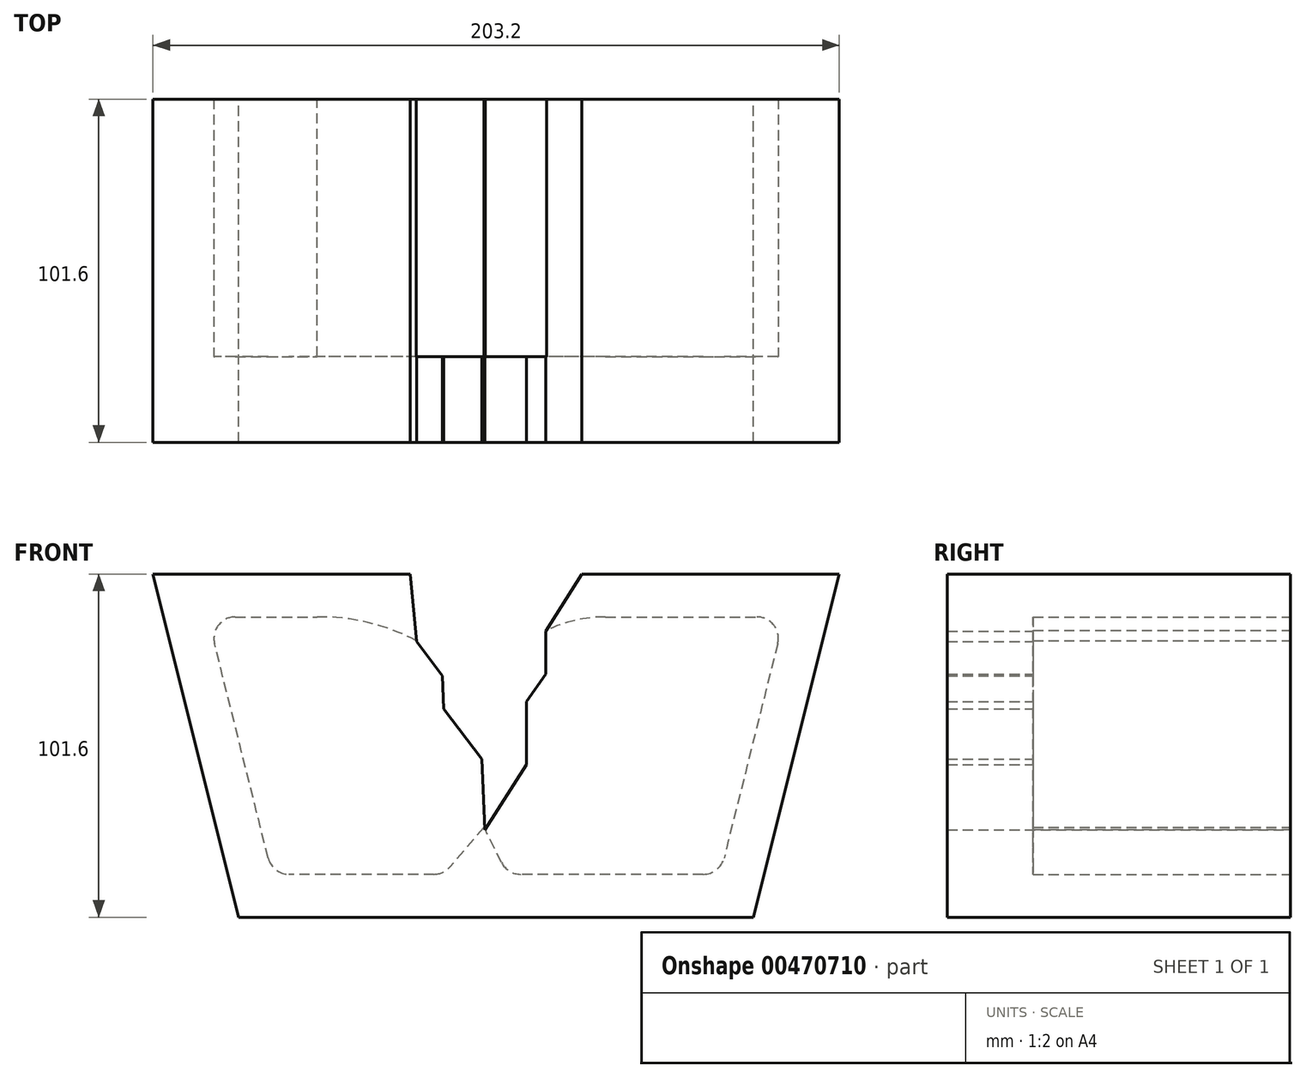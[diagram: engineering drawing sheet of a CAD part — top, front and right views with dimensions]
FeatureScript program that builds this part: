
annotation { "Feature Type Name" : "Feature", "Feature Type Description" : "" }
export const myFeature = defineFeature(function(context is Context, id is Id, definition is map)
    precondition{}
    {
        {
            var Q0;
            Q0=qCreatedBy(makeId("Front.planeOp"),FACE);
            var sketch = newSketch(context, id + "F0", { "sketchPlane" : qUnion([Q0])});
            skLineSegment(sketch, "E0", {"start": v(-97.99, 50.2) * mm, "end": v(-21.79, 50.2) * mm});
            skLineSegment(sketch, "E1", {"start": v(105.21, 50.2) * mm, "end": v(79.81, -51.4) * mm});
            skLineSegment(sketch, "E2", {"start": v(79.81, -51.4) * mm, "end": v(-72.59, -51.4) * mm});
            skLineSegment(sketch, "E3", {"start": v(-72.59, -51.4) * mm, "end": v(-97.99, 50.2) * mm});
            skPoint(sketch, "E4", {"position": v(29.01, 50.2) * mm});
            skPoint(sketch, "E5", {"position": v(-21.79, 50.2) * mm});
            skLineSegment(sketch, "E6", {"start": v(29.01, 50.2) * mm, "end": v(18.3, 33.19) * mm});
            skLineSegment(sketch, "E7", {"start": v(18.3, 33.19) * mm, "end": v(18.3, 20.5) * mm});
            skLineSegment(sketch, "E8", {"start": v(18.3, 20.5) * mm, "end": v(12.63, 12.48) * mm});
            skLineSegment(sketch, "E9", {"start": v(12.63, 12.48) * mm, "end": v(12.63, -6.22) * mm});
            skLineSegment(sketch, "E10", {"start": v(12.63, -6.22) * mm, "end": v(0, -26) * mm});
            skLineSegment(sketch, "E11", {"start": v(-21.79, 50.2) * mm, "end": v(-19.97, 30.18) * mm});
            skLineSegment(sketch, "E12", {"start": v(-19.97, 30.18) * mm, "end": v(-12.26, 20.1) * mm});
            skLineSegment(sketch, "E13", {"start": v(-12.26, 20.1) * mm, "end": v(-11.9, 10.28) * mm});
            skLineSegment(sketch, "E14", {"start": v(-11.9, 10.28) * mm, "end": v(-0.55, -4.57) * mm});
            skLineSegment(sketch, "E15", {"start": v(-0.55, -4.57) * mm, "end": v(0.31, -26) * mm});
            skLineSegment(sketch, "E16.trimOffspring", {"start": v(29.01, 50.2) * mm, "end": v(105.21, 50.2) * mm});
            skSolve(sketch);
        }
        {
            var Q0;
            Q0=makeQuery(id+"F0.imprint","IMPRINT",FACE,{"disambiguationData":[TD([[makeQuery(id+"F0.imprint","IMPRINT",EDGE,{"derivedFrom":sQuery(id+"F0.wireOp",EDGE,"E0")}),-1.0]])]});
            extrude(context, id + "F1", {"entities" : qUnion([Q0]), "depth" : 101.6 * mm});
        }
        {
            var Q0;
            Q0=qCreatedBy(makeId("Front.planeOp"),FACE);
            var sketch = newSketch(context, id + "F2", { "sketchPlane" : qUnion([Q0])});
            skLineSegment(sketch, "E17.2", {"start": v(-81.72, 37.5) * mm, "end": v(-49.43, 37.5) * mm});
            skLineSegment(sketch, "E17.3", {"start": v(36.02, 37.5) * mm, "end": v(88.94, 37.5) * mm});
            skLineSegment(sketch, "E17.7", {"start": v(88.94, 37.5) * mm, "end": v(69.9, -38.7) * mm});
            skLineSegment(sketch, "E17.11", {"start": v(-11.88, -38.7) * mm, "end": v(-62.67, -38.7) * mm});
            skLineSegment(sketch, "E17.12", {"start": v(69.9, -38.7) * mm, "end": v(6.96, -38.7) * mm});
            skLineSegment(sketch, "E17.14", {"start": v(-62.67, -38.7) * mm, "end": v(-81.72, 37.5) * mm});
            skLineSegment(sketch, "E18", {"start": v(6.96, -38.7) * mm, "end": v(0, -24.79) * mm});
            skLineSegment(sketch, "E19", {"start": v(0, -24.79) * mm, "end": v(-11.88, -38.7) * mm});
            skLineSegment(sketch, "E20", {"start": v(18.5, 33.5) * mm, "end": v(-20, 30.45) * mm});
            skArc(sketch, "E21", {"start": v(-20, 30.45) * mm, "mid": v(-34.27, 35.82) * mm, "end": v(-49.43, 37.5) * mm});
            skArc(sketch, "E22", {"start": v(36.02, 37.5) * mm, "mid": v(27.04, 36.49) * mm, "end": v(18.5, 33.5) * mm});
            skSolve(sketch);
        }
        {
            var Q0;
            Q0=makeQuery(id+"F2.imprint","IMPRINT",FACE,{"disambiguationData":[TD([[makeQuery(id+"F2.imprint","IMPRINT",EDGE,{"derivedFrom":sQuery(id+"F2.wireOp",EDGE,"E17.2")}),-1.0]])]});
            extrude(context, id + "F3", {"entities" : qUnion([Q0]), "operationType" : NewBodyOperationType.REMOVE, "depth" : 76.2 * mm});
        }
        {
            var Q0;
            Q0=makeQuery(id+"F3.boolean.opBoolean","COPY",EDGE,{"derivedFrom":makeQuery(id+"F3.opExtrude","SWEPT_EDGE",EDGE,{"disambiguationData":[OSD([sQuery(id+"F2.wireOp",EDGE,"E17.11"),sQuery(id+"F2.wireOp",EDGE,"E19")])]})});
            var Q1;
            Q1=makeQuery(id+"F3.boolean.opBoolean","COPY",EDGE,{"derivedFrom":makeQuery(id+"F3.opExtrude","SWEPT_EDGE",EDGE,{"disambiguationData":[OSD([sQuery(id+"F2.wireOp",EDGE,"E17.12"),sQuery(id+"F2.wireOp",EDGE,"E18")])]})});
            var Q2;
            Q2=makeQuery(id+"F3.boolean.opBoolean","COPY",EDGE,{"derivedFrom":makeQuery(id+"F3.opExtrude","SWEPT_EDGE",EDGE,{"disambiguationData":[OSD([sQuery(id+"F2.wireOp",EDGE,"E17.11"),sQuery(id+"F2.wireOp",EDGE,"E17.14")])]})});
            var Q3;
            Q3=makeQuery(id+"F3.boolean.opBoolean","COPY",EDGE,{"derivedFrom":makeQuery(id+"F3.opExtrude","SWEPT_EDGE",EDGE,{"disambiguationData":[OSD([sQuery(id+"F2.wireOp",EDGE,"E17.7"),sQuery(id+"F2.wireOp",EDGE,"E17.12")])]})});
            var Q4;
            Q4=makeQuery(id+"F3.boolean.opBoolean","COPY",EDGE,{"derivedFrom":makeQuery(id+"F3.opExtrude","SWEPT_EDGE",EDGE,{"disambiguationData":[OSD([sQuery(id+"F2.wireOp",EDGE,"E17.3"),sQuery(id+"F2.wireOp",EDGE,"E17.7")])]})});
            var Q5;
            Q5=makeQuery(id+"F3.boolean.opBoolean","COPY",EDGE,{"derivedFrom":makeQuery(id+"F3.opExtrude","SWEPT_EDGE",EDGE,{"disambiguationData":[OSD([sQuery(id+"F2.wireOp",EDGE,"E17.2"),sQuery(id+"F2.wireOp",EDGE,"E17.14")])]})});
            fillet(context, id + "F4", {"entities" : qUnion([Q0, Q1, Q2, Q3, Q4, Q5]), "radius" : 6.35 * mm, "tangentPropagation" : true, "allowEdgeOverflow" : false});
        }
    });
